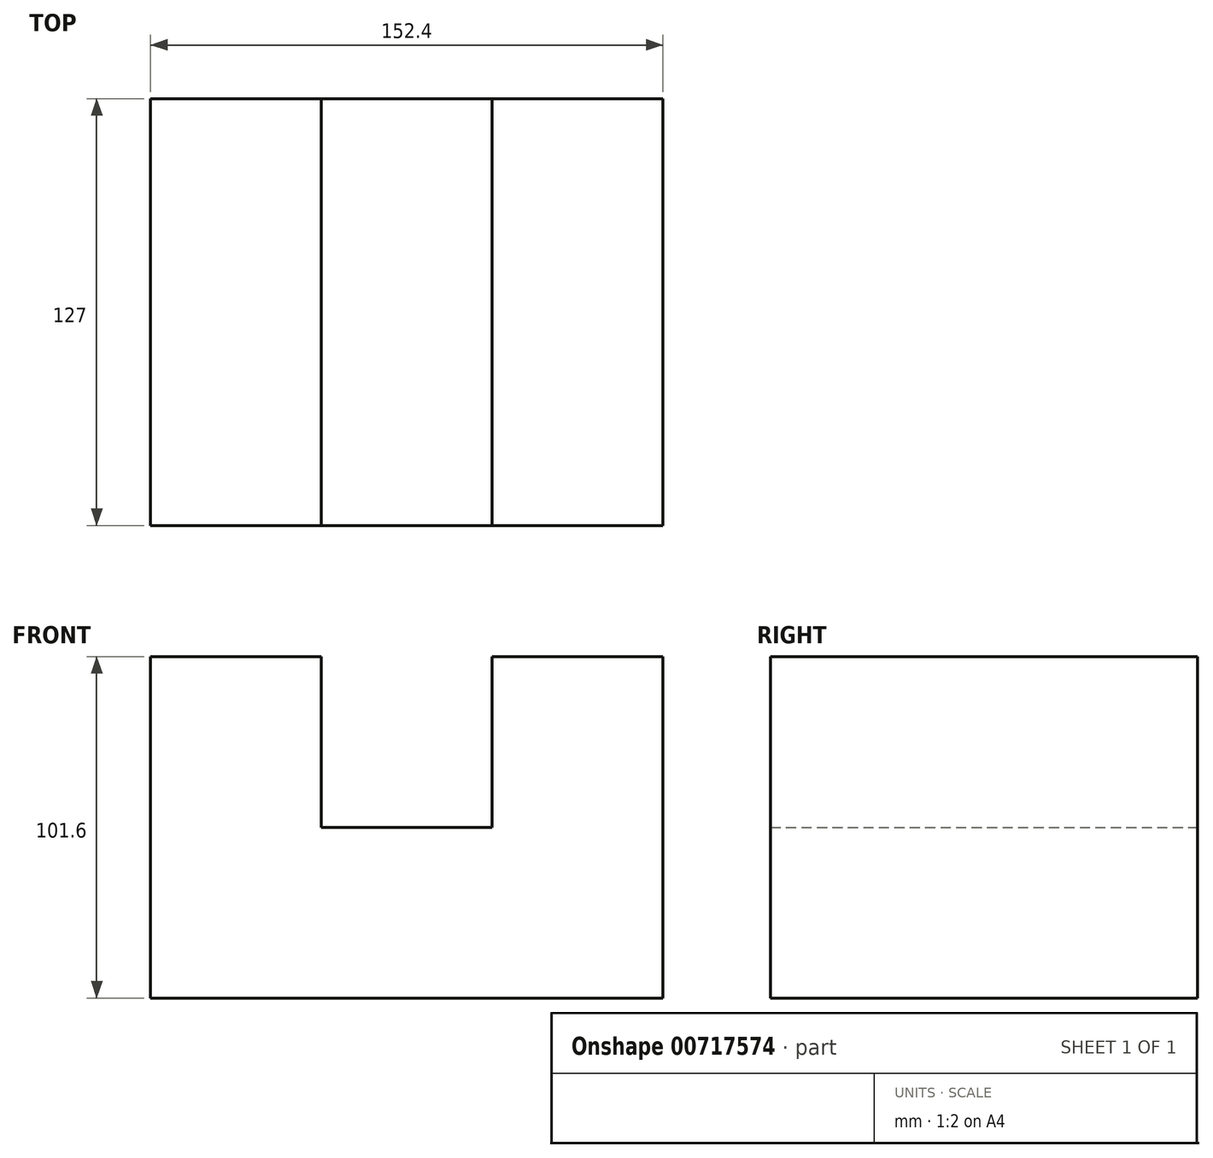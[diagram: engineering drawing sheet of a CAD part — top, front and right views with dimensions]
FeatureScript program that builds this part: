
annotation { "Feature Type Name" : "Feature", "Feature Type Description" : "" }
export const myFeature = defineFeature(function(context is Context, id is Id, definition is map)
    precondition{}
    {
        {
            var Q0;
            Q0=qCreatedBy(makeId("Front.planeOp"),FACE);
            var sketch = newSketch(context, id + "F0", { "sketchPlane" : qUnion([Q0])});
            skLineSegment(sketch, "E0", {"start": v(-101.6, -36.11) * mm, "end": v(-101.6, 65.49) * mm});
            skLineSegment(sketch, "E1", {"start": v(-101.6, -36.11) * mm, "end": v(50.8, -36.11) * mm});
            skLineSegment(sketch, "E2", {"start": v(50.8, -36.11) * mm, "end": v(50.8, 65.49) * mm});
            skLineSegment(sketch, "E3", {"start": v(50.8, 65.49) * mm, "end": v(0, 65.49) * mm});
            skLineSegment(sketch, "E4", {"start": v(0, 65.49) * mm, "end": v(0, 14.69) * mm});
            skLineSegment(sketch, "E5", {"start": v(0, 14.69) * mm, "end": v(-50.8, 14.69) * mm});
            skLineSegment(sketch, "E6", {"start": v(-101.6, 65.49) * mm, "end": v(-50.8, 65.49) * mm});
            skLineSegment(sketch, "E7", {"start": v(-50.8, 65.49) * mm, "end": v(-50.8, 14.69) * mm});
            skSolve(sketch);
        }
        {
            var Q0;
            Q0=makeQuery(id+"F0.imprint","IMPRINT",FACE,{"disambiguationData":[TD([[makeQuery(id+"F0.imprint","IMPRINT",EDGE,{"derivedFrom":sQuery(id+"F0.wireOp",EDGE,"E0")}),-1.0]])]});
            extrude(context, id + "F1", {"entities" : qUnion([Q0]), "depth" : 127 * mm, "offsetDistance" : 25.4 * mm});
        }
    });
